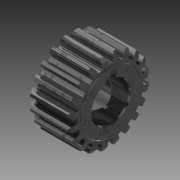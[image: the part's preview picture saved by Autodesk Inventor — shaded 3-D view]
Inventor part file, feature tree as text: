
AUTODESK INVENTOR PART (.ipt)
format: ipt  version: 2013 (Build 170138000, 138)  size: 365,056 bytes
history: native  units: mm (DEFAULTED — no unit token found)
features: extrude x4, sketch x4, chamfer x3, other x1, fillet x1
ambient origin geometry x8: Origin, YZ Plane, XZ Plane, XY Plane, X Axis, Y Axis, Z Axis, Center Point
bodies: Solid1 (feature_tree)
feature tree (13):
  other  "Gear Blank"
  extrude  "Tooth Profile"  Depth=24.59095mm
  chamfer  "Bore Chamfer Interior"  Distance=12.7mm
  extrude  "Hub"  Depth=12.7mm
  fillet  "Hub Fillet"  Radius=25.4mm
  chamfer  "Bore Chamfer Exterior"  Distance=200.0mm
  chamfer  "Bore Chamfer on Hub"  Distance=0.381mm
  extrude  "Hex Broach"  Depth=0.381mm
  extrude  "Key"  Depth=0.381mm
  sketch  "Sketch2"  dims[d12=90.0deg d24=24.59095mm]
  sketch  "Sketch3"  dims[d26=0.0mm]
  sketch  "Sketch5"  dims[d31=20.32mm]
  sketch  "Sketch16"  dims[d32=0.254mm d77=12.7mm d78=12.7mm d79=25.4mm d83=200.0mm d95=0.381mm d96=3.175mm d97=0.381mm d98=3.175mm d99=0.381mm d100=3.175mm d104=13.97mm d108=30.0deg d109=30.0deg d110=14.224mm d112=0.254mm d117=3.175mm d118=4.7625mm d119=25.4mm d120=0.0mm d121=45.0deg d122=45.0deg d123=45.0deg]
